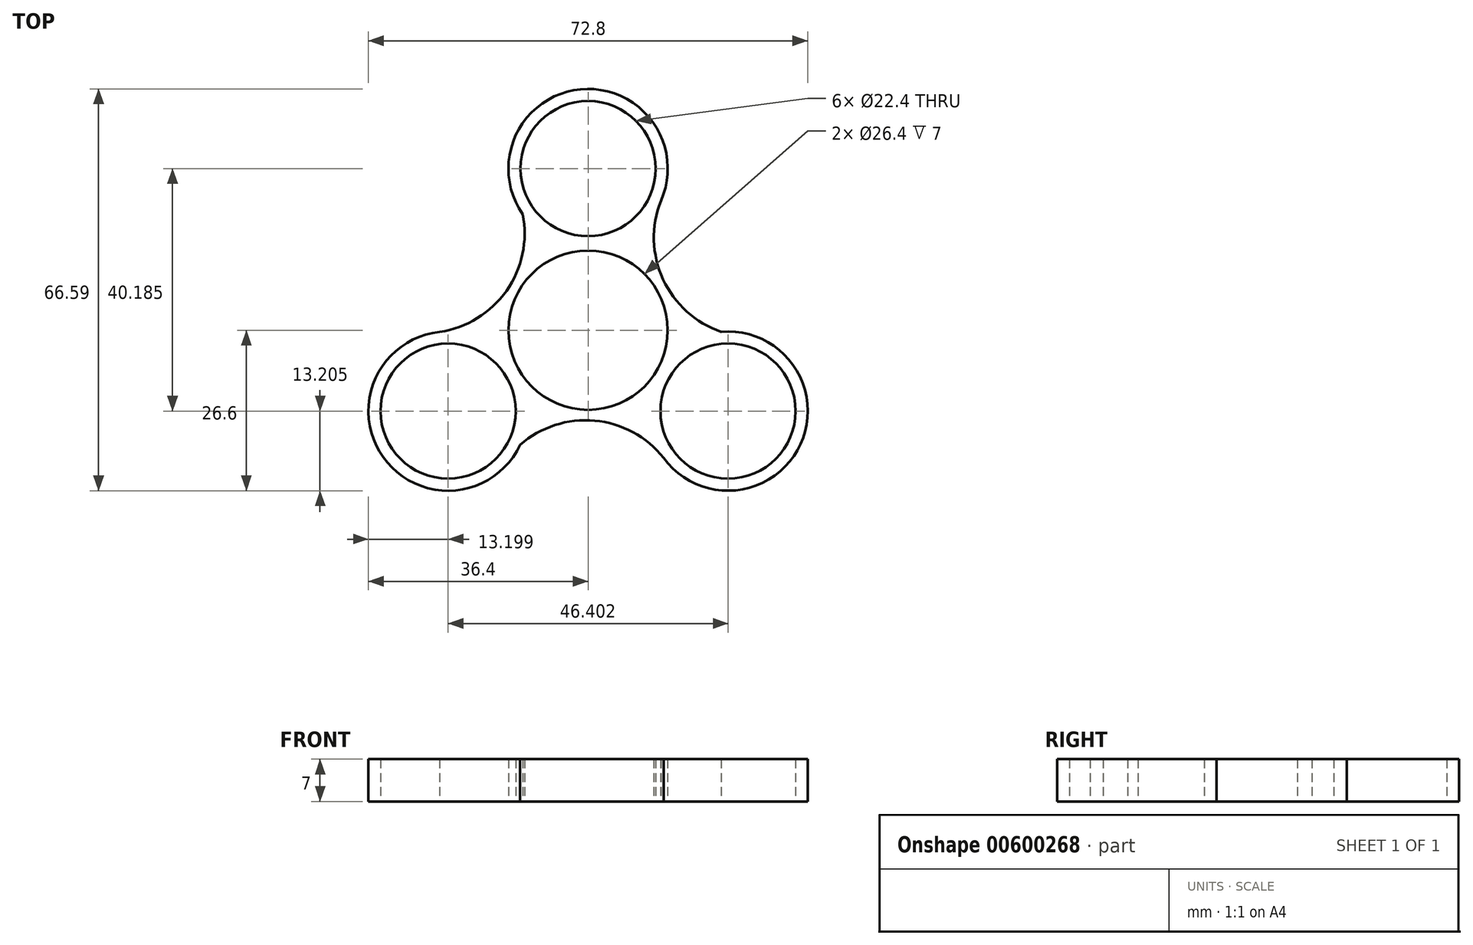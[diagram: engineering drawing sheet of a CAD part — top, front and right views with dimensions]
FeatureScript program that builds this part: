
annotation { "Feature Type Name" : "Feature", "Feature Type Description" : "" }
export const myFeature = defineFeature(function(context is Context, id is Id, definition is map)
    precondition{}
    {
        {
            var Q0;
            Q0=qCreatedBy(makeId("Top.planeOp"),FACE);
            var sketch = newSketch(context, id + "F0", { "sketchPlane" : qUnion([Q0])});
            skCircle(sketch, "E0", {"center": v(0, 0) * mm, "radius": 11.2 * mm});
            skCircle(sketch, "E1", {"center": v(0, 0) * mm, "radius": 13.2 * mm});
            skCircle(sketch, "E2", {"center": v(0, 26.8) * mm, "radius": 11.2 * mm});
            skArc(sketch, "E3", {"start": v(12.06, 21.42) * mm, "mid": v(-1.25, 39.93) * mm, "end": v(-10.83, 19.24) * mm});
            skCircle(sketch, "E4.1.0", {"center": v(-23.2, -13.4) * mm, "radius": 11.2 * mm});
            skArc(sketch, "E4.1.1", {"start": v(-24.58, -0.27) * mm, "mid": v(-33.95, -21.05) * mm, "end": v(-11.25, -19) * mm});
            skCircle(sketch, "E4.2.0", {"center": v(23.2, -13.4) * mm, "radius": 11.2 * mm});
            skArc(sketch, "E4.2.1", {"start": v(12.52, -21.16) * mm, "mid": v(35.2, -18.88) * mm, "end": v(22.08, -0.24) * mm});
            skArc(sketch, "E5", {"start": v(12.06, 21.42) * mm, "mid": v(12.43, 8.45) * mm, "end": v(22.08, -0.24) * mm});
            skArc(sketch, "E6.1.0", {"start": v(-24.58, -0.27) * mm, "mid": v(-13.53, 6.54) * mm, "end": v(-10.83, 19.24) * mm});
            skArc(sketch, "E6.2.0", {"start": v(12.52, -21.16) * mm, "mid": v(1.1, -14.99) * mm, "end": v(-11.25, -19) * mm});
            skSolve(sketch);
        }
        {
            var Q0;
            Q0=makeQuery(id+"F0.imprint","IMPRINT",FACE,{"disambiguationData":[TD([[makeQuery(id+"F0.imprint","IMPRINT",EDGE,{"derivedFrom":sQuery(id+"F0.wireOp",EDGE,"E1")}),-1.0]])]});
            extrude(context, id + "F1", {"entities" : qUnion([Q0]), "depth" : 7 * mm, "offsetDistance" : 25 * mm});
        }
    });
